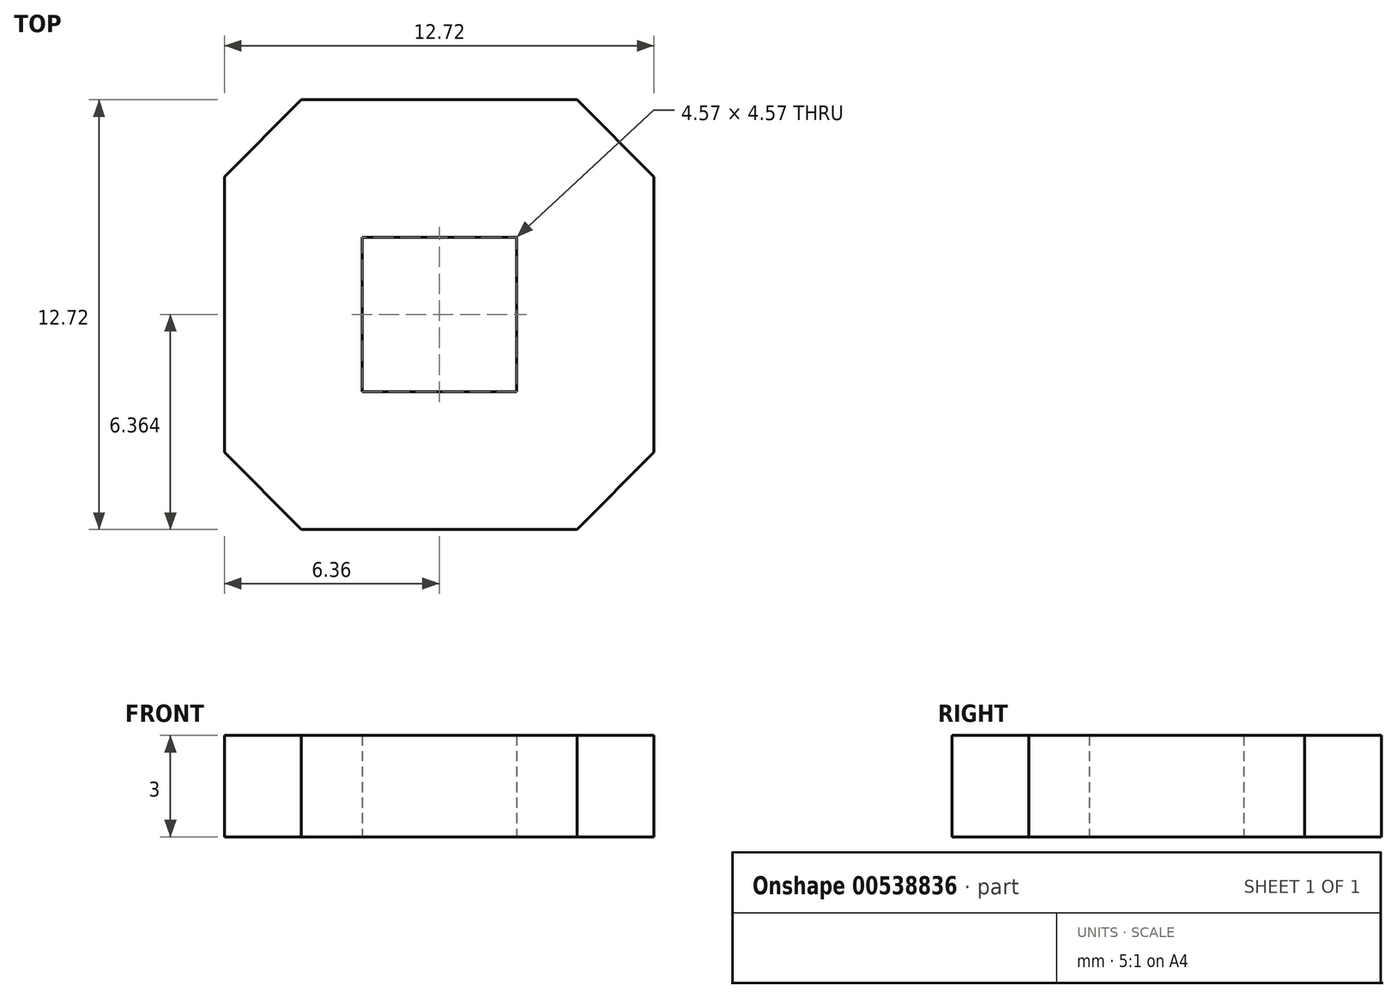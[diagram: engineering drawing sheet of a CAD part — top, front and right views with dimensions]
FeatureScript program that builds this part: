
annotation { "Feature Type Name" : "Feature", "Feature Type Description" : "" }
export const myFeature = defineFeature(function(context is Context, id is Id, definition is map)
    precondition{}
    {
        {
            var Q0;
            Q0=qCreatedBy(makeId("Top.planeOp"),FACE);
            var sketch = newSketch(context, id + "F0", { "sketchPlane" : qUnion([Q0])});
            skLineSegment(sketch, "E0", {"start": v(-4.1, 6.75) * mm, "end": v(4.07, 6.75) * mm});
            skLineSegment(sketch, "E1", {"start": v(4.07, 6.75) * mm, "end": v(6.35, 4.47) * mm});
            skLineSegment(sketch, "E2", {"start": v(6.35, 4.47) * mm, "end": v(6.35, -3.69) * mm});
            skLineSegment(sketch, "E3", {"start": v(6.35, -3.69) * mm, "end": v(4.07, -5.97) * mm});
            skLineSegment(sketch, "E4", {"start": v(4.07, -5.97) * mm, "end": v(-4.1, -5.97) * mm});
            skLineSegment(sketch, "E5", {"start": v(-4.1, -5.97) * mm, "end": v(-6.37, -3.69) * mm});
            skLineSegment(sketch, "E6", {"start": v(-6.37, -3.69) * mm, "end": v(-6.37, 4.47) * mm});
            skLineSegment(sketch, "E7", {"start": v(-6.37, 4.47) * mm, "end": v(-4.1, 6.75) * mm});
            skLineSegment(sketch, "E8.bottom", {"start": v(-2.3, 2.68) * mm, "end": v(2.28, 2.68) * mm});
            skLineSegment(sketch, "E8.top", {"start": v(-2.3, -1.9) * mm, "end": v(2.28, -1.9) * mm});
            skLineSegment(sketch, "E8.left", {"start": v(-2.3, 2.68) * mm, "end": v(-2.3, -1.9) * mm});
            skLineSegment(sketch, "E8.right", {"start": v(2.28, 2.68) * mm, "end": v(2.28, -1.9) * mm});
            skLineSegment(sketch, "E9", {"start": v(2.28, 2.68) * mm, "end": v(6.35, 4.47) * mm});
            skLineSegment(sketch, "E10", {"start": v(-6.37, 4.47) * mm, "end": v(-2.3, 2.68) * mm});
            skLineSegment(sketch, "E11", {"start": v(-2.3, -1.9) * mm, "end": v(-6.37, -3.69) * mm});
            skLineSegment(sketch, "E12", {"start": v(2.28, -1.9) * mm, "end": v(6.35, -3.69) * mm});
            skSolve(sketch);
        }
        {
            var Q0;
            Q0=makeQuery(id+"F0.imprint","IMPRINT",FACE,{"disambiguationData":[TD([[makeQuery(id+"F0.imprint","IMPRINT",EDGE,{"derivedFrom":sQuery(id+"F0.wireOp",EDGE,"E3")}),-1.0]])]});
            var Q1;
            Q1=makeQuery(id+"F0.imprint","IMPRINT",FACE,{"disambiguationData":[TD([[makeQuery(id+"F0.imprint","IMPRINT",EDGE,{"derivedFrom":sQuery(id+"F0.wireOp",EDGE,"E2")}),-1.0]])]});
            var Q2;
            Q2=makeQuery(id+"F0.imprint","IMPRINT",FACE,{"disambiguationData":[TD([[makeQuery(id+"F0.imprint","IMPRINT",EDGE,{"derivedFrom":sQuery(id+"F0.wireOp",EDGE,"E6")}),-1.0]])]});
            var Q3;
            Q3=makeQuery(id+"F0.imprint","IMPRINT",FACE,{"disambiguationData":[TD([[makeQuery(id+"F0.imprint","IMPRINT",EDGE,{"derivedFrom":sQuery(id+"F0.wireOp",EDGE,"E0")}),-1.0]])]});
            extrude(context, id + "F1", {"entities" : qUnion([Q0, Q1, Q2, Q3]), "depth" : 3 * mm, "offsetDistance" : 25 * mm});
        }
    });
